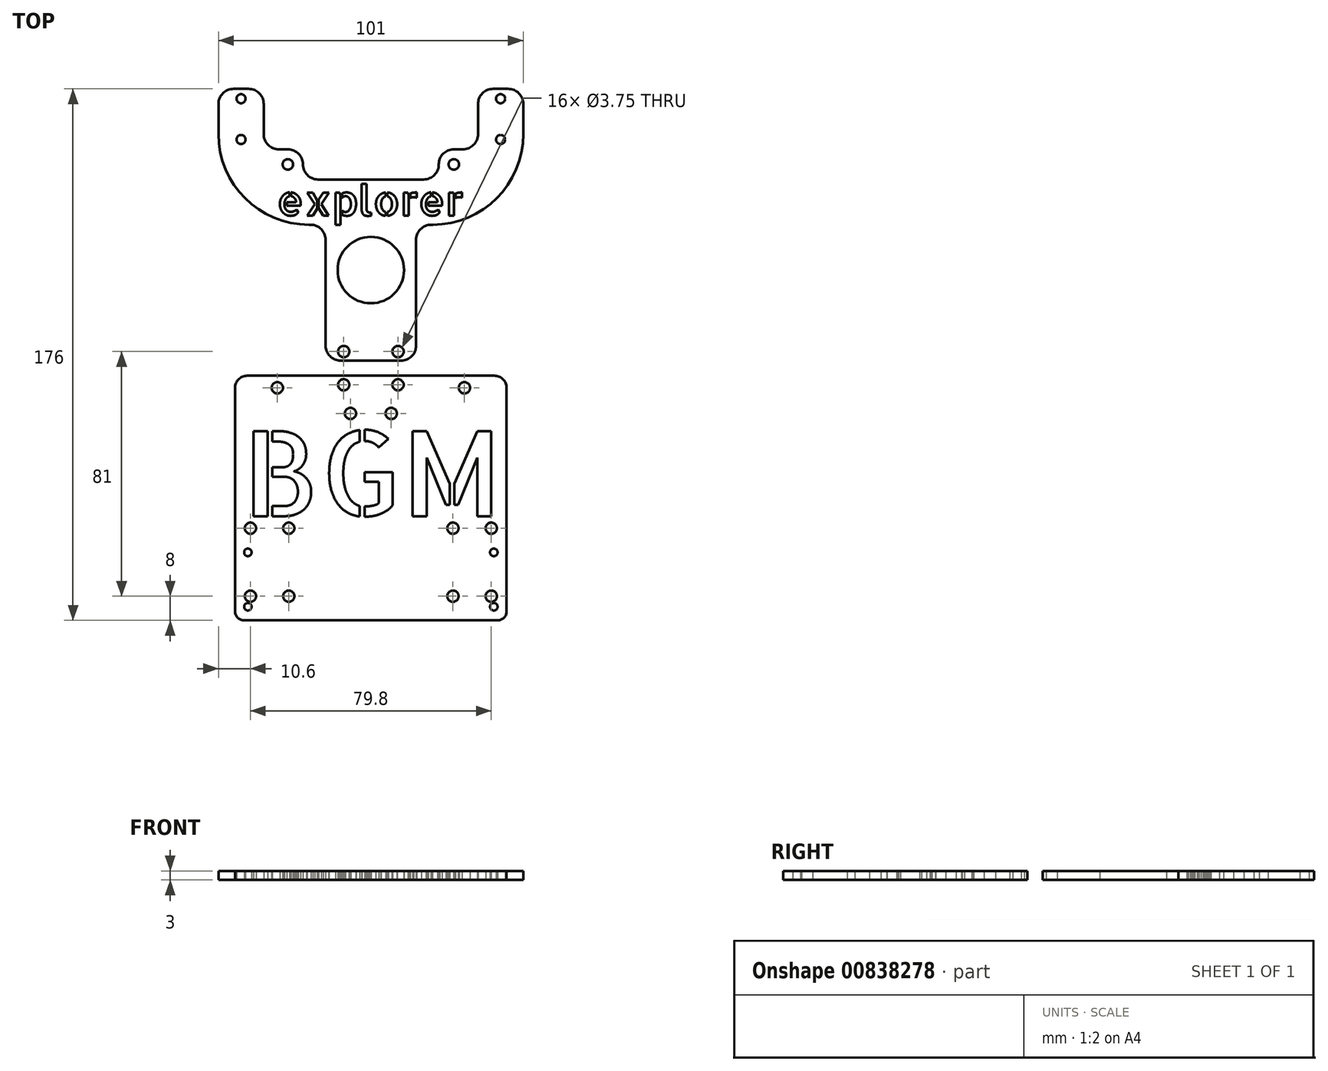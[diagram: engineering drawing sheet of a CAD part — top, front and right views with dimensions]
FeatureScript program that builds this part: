
annotation { "Feature Type Name" : "Feature", "Feature Type Description" : "" }
export const myFeature = defineFeature(function(context is Context, id is Id, definition is map)
    precondition{}
    {
        {
            var Q0;
            Q0=qCreatedBy(makeId("Top.planeOp"),FACE);
            var sketch = newSketch(context, id + "F0", { "sketchPlane" : qUnion([Q0])});
            skLineSegment(sketch, "E0.bottom", {"start": v(-45, -40.5) * mm, "end": v(45, -40.5) * mm});
            skLineSegment(sketch, "E0.top", {"start": v(-45, 40.5) * mm, "end": v(45, 40.5) * mm});
            skLineSegment(sketch, "E0.left", {"start": v(-45, -40.5) * mm, "end": v(-45, 40.5) * mm});
            skLineSegment(sketch, "E0.right", {"start": v(45, -40.5) * mm, "end": v(45, 40.5) * mm});
            skPoint(sketch, "E0.middle", {"position": v(0, 0) * mm});
            skCircle(sketch, "E1", {"center": v(-39.9, -32.5) * mm, "radius": 1.88 * mm});
            skCircle(sketch, "E2", {"center": v(-39.9, -10) * mm, "radius": 1.88 * mm});
            skCircle(sketch, "E3", {"center": v(-27.2, -10) * mm, "radius": 1.88 * mm});
            skCircle(sketch, "E4", {"center": v(-27.2, -32.5) * mm, "radius": 1.88 * mm});
            skCircle(sketch, "E5", {"center": v(-9, 37.5) * mm, "radius": 1.88 * mm});
            skCircle(sketch, "E6", {"center": v(-31, 36.5) * mm, "radius": 1.88 * mm});
            skLineSegment(sketch, "E7", {"start": v(0, 40.5) * mm, "end": v(0, -40.5) * mm, "construction": true});
            skCircle(sketch, "E8.MirrorC", {"center": v(27.2, -32.5) * mm, "radius": 1.88 * mm});
            skCircle(sketch, "E9.MirrorC", {"center": v(27.2, -10) * mm, "radius": 1.88 * mm});
            skCircle(sketch, "E10.MirrorC", {"center": v(39.9, -32.5) * mm, "radius": 1.88 * mm});
            skCircle(sketch, "E11.MirrorC", {"center": v(31, 36.5) * mm, "radius": 1.88 * mm});
            skCircle(sketch, "E12.MirrorC", {"center": v(39.9, -10) * mm, "radius": 1.88 * mm});
            skCircle(sketch, "E13.MirrorC", {"center": v(9, 37.5) * mm, "radius": 1.88 * mm});
            skText(sketch, "E14", { "text": "BGM", "fontName": "AllertaStencil-Regular.ttf"});
            skCircle(sketch, "E15", {"center": v(-6.75, 28) * mm, "radius": 1.88 * mm});
            skCircle(sketch, "E16.MirrorC", {"center": v(6.75, 28) * mm, "radius": 1.88 * mm});
            skCircle(sketch, "E17", {"center": v(-40.75, -36) * mm, "radius": 1.25 * mm});
            skCircle(sketch, "E18", {"center": v(-40.75, -18) * mm, "radius": 1.25 * mm});
            skCircle(sketch, "E19.MirrorC", {"center": v(40.75, -18) * mm, "radius": 1.25 * mm});
            skCircle(sketch, "E20.MirrorC", {"center": v(40.75, -36) * mm, "radius": 1.25 * mm});
            const initialGuessF0  = {"E14": [-0.0425, -0.006, 1, 0, 0.0282]};
            skSetInitialGuess(sketch, initialGuessF0);
            skSolve(sketch);
        }
        {
            var Q0;
            Q0=makeQuery(id+"F0.imprint","IMPRINT",FACE,{"disambiguationData":[TD([[makeQuery(id+"F0.imprint","IMPRINT",EDGE,{"derivedFrom":sQuery(id+"F0.wireOp",EDGE,"E0.bottom")}),1.0]])]});
            var Q1;
            {var subQ5=sQuery(id+"F0.wireOp",EDGE,"2Zm90AiD-Dhtj-uD5s-axWy-PgKTOK4LKh8v.bottom");Q1=makeQuery(id+"F0.imprint","IMPRINT",FACE,{"disambiguationData":[TD([[makeQuery(id+"F0.imprint","IMPRINT",EDGE,{"derivedFrom":subQ5}),1.0]])]});}
            var Q2;
            {var subQ0=sQuery(id+"F0.wireOp",EDGE,"E14.sketch_text.stroke-19");Q2=makeQuery(id+"F0.imprint","IMPRINT",FACE,{"disambiguationData":[TD([[makeQuery(id+"F0.imprint","IMPRINT",EDGE,{"derivedFrom":subQ0}),1.0]])]});}
            var Q3;
            {var subQ1=sQuery(id+"F0.wireOp",EDGE,"E14.sketch_text.stroke-21");Q3=makeQuery(id+"F0.imprint","IMPRINT",FACE,{"disambiguationData":[TD([[makeQuery(id+"F0.imprint","IMPRINT",EDGE,{"derivedFrom":subQ1}),1.0]])]});}
            var Q4;
            {var subQ1=sQuery(id+"F0.wireOp",EDGE,"E14.sketch_text.stroke-17");Q4=makeQuery(id+"F0.imprint","IMPRINT",FACE,{"disambiguationData":[TD([[makeQuery(id+"F0.imprint","IMPRINT",EDGE,{"derivedFrom":subQ1}),1.0]])]});}
            var Q5;
            {var subQ1=sQuery(id+"F0.wireOp",EDGE,"E14.sketch_text.stroke-13");Q5=makeQuery(id+"F0.imprint","IMPRINT",FACE,{"disambiguationData":[TD([[makeQuery(id+"F0.imprint","IMPRINT",EDGE,{"derivedFrom":subQ1}),1.0]])]});}
            var Q6;
            {var subQ1=sQuery(id+"F0.wireOp",EDGE,"2Zm90AiD-Dhtj-uD5s-axWy-PgKTOK4LKh8v.top");Q6=makeQuery(id+"F0.imprint","IMPRINT",FACE,{"disambiguationData":[TD([[makeQuery(id+"F0.imprint","IMPRINT",EDGE,{"derivedFrom":subQ1}),-1.0]])]});}
            extrude(context, id + "F1", {"entities" : qUnion([Q0, Q1, Q2, Q3, Q4, Q5, Q6]), "depth" : 3 * mm, "offsetDistance" : 25 * mm});
        }
        {
            var Q0;
            Q0=makeQuery(id+"F1.opExtrude","SWEPT_EDGE",EDGE,{"disambiguationData":[OSD([sQuery(id+"F0.wireOp",EDGE,"E0.top"),sQuery(id+"F0.wireOp",EDGE,"EnCkEkhA-jMUl-QUfc-oNYT-XxU6Z7l8rYp0")])]});
            var Q1;
            Q1=makeQuery(id+"F1.opExtrude","SWEPT_EDGE",EDGE,{"disambiguationData":[OSD([sQuery(id+"F0.wireOp",EDGE,"QOfj2mfs-kfRg-gTgU-dF6D-Hk0wWBTF9spk"),sQuery(id+"F0.wireOp",EDGE,"EnCkEkhA-jMUl-QUfc-oNYT-XxU6Z7l8rYp0")])]});
            var Q2;
            Q2=makeQuery(id+"F1.opExtrude","SWEPT_EDGE",EDGE,{"disambiguationData":[OSD([sQuery(id+"F0.wireOp",EDGE,"E0.top"),sQuery(id+"F0.wireOp",EDGE,"c5541e3c-3a26-47a1-8419-0039d4e5da4d0.MirrorCS")])]});
            var Q3;
            Q3=makeQuery(id+"F1.opExtrude","SWEPT_EDGE",EDGE,{"disambiguationData":[OSD([sQuery(id+"F0.wireOp",EDGE,"c5541e3c-3a26-47a1-8419-0039d4e5da4d0.MirrorCS"),sQuery(id+"F0.wireOp",EDGE,"c5541e3c-3a26-47a1-8419-0039d4e5da4d1.MirrorCS")])]});
            fillet(context, id + "F2", {"entities" : qUnion([Q0, Q1, Q2, Q3]), "radius" : 4 * mm, "tangentPropagation" : true, "allowEdgeOverflow" : false});
        }
        {
            var Q0;
            Q0=makeQuery(id+"F1.opExtrude","SWEPT_EDGE",EDGE,{"disambiguationData":[OSD([sQuery(id+"F0.wireOp",EDGE,"E0.bottom"),sQuery(id+"F0.wireOp",EDGE,"E0.left")])]});
            var Q1;
            Q1=makeQuery(id+"F1.opExtrude","SWEPT_EDGE",EDGE,{"disambiguationData":[OSD([sQuery(id+"F0.wireOp",EDGE,"E0.bottom"),sQuery(id+"F0.wireOp",EDGE,"E0.right")])]});
            fillet(context, id + "F3", {"entities" : qUnion([Q0, Q1]), "radius" : 3 * mm, "tangentPropagation" : true, "allowEdgeOverflow" : false});
        }
        {
            var Q0;
            Q0=qCreatedBy(makeId("Top.planeOp"),FACE);
            var sketch = newSketch(context, id + "F4", { "sketchPlane" : qUnion([Q0])});
            skLineSegment(sketch, "E21", {"start": v(-22.5, 115.5) * mm, "end": v(-35.5, 115.5) * mm});
            skLineSegment(sketch, "E22", {"start": v(35.5, 115.5) * mm, "end": v(22.5, 115.5) * mm});
            skLineSegment(sketch, "E23", {"start": v(22.5, 115.5) * mm, "end": v(22.5, 105.5) * mm});
            skLineSegment(sketch, "E24", {"start": v(22.5, 105.5) * mm, "end": v(0, 105.5) * mm});
            skLineSegment(sketch, "E25", {"start": v(-22.5, 105.5) * mm, "end": v(-22.5, 115.5) * mm});
            skLineSegment(sketch, "E26", {"start": v(0, 105.5) * mm, "end": v(-22.5, 105.5) * mm});
            skCircle(sketch, "E27", {"center": v(-27.5, 110.5) * mm, "radius": 1.75 * mm});
            skCircle(sketch, "E28", {"center": v(27.5, 110.5) * mm, "radius": 1.75 * mm});
            skCircle(sketch, "E29", {"center": v(0, 75.5) * mm, "radius": 11 * mm});
            skLineSegment(sketch, "E30", {"start": v(0, 75.5) * mm, "end": v(0, 105.5) * mm, "construction": true});
            skLineSegment(sketch, "E31", {"start": v(0, 75.5) * mm, "end": v(0, 45.5) * mm, "construction": true});
            skLineSegment(sketch, "E32.0", {"start": v(-41, 40.5) * mm, "end": v(0, 40.5) * mm});
            skCircle(sketch, "E33.0", {"center": v(-9, 37.5) * mm, "radius": 1.88 * mm});
            skCircle(sketch, "E34.0", {"center": v(9, 37.5) * mm, "radius": 1.88 * mm});
            skCircle(sketch, "E35", {"center": v(-9, 48.5) * mm, "radius": 1.88 * mm});
            skCircle(sketch, "E36", {"center": v(9, 48.5) * mm, "radius": 1.88 * mm});
            skLineSegment(sketch, "E37", {"start": v(0, 45.5) * mm, "end": v(-15, 45.5) * mm});
            skLineSegment(sketch, "E38", {"start": v(0, 45.5) * mm, "end": v(15, 45.5) * mm});
            skLineSegment(sketch, "E39", {"start": v(0, 40.5) * mm, "end": v(41, 40.5) * mm});
            skLineSegment(sketch, "E40", {"start": v(-15, 45.5) * mm, "end": v(-15, 90.5) * mm});
            skLineSegment(sketch, "E41", {"start": v(-15, 90.5) * mm, "end": v(-50.5, 90.5) * mm});
            skLineSegment(sketch, "E42", {"start": v(-50.5, 90.5) * mm, "end": v(-50.5, 135.5) * mm});
            skLineSegment(sketch, "E43", {"start": v(-35.5, 115.5) * mm, "end": v(-35.5, 135.5) * mm});
            skLineSegment(sketch, "E44", {"start": v(-35.5, 135.5) * mm, "end": v(-50.5, 135.5) * mm});
            skLineSegment(sketch, "E45", {"start": v(35.5, 115.5) * mm, "end": v(35.5, 135.5) * mm});
            skLineSegment(sketch, "E46", {"start": v(35.5, 135.5) * mm, "end": v(50.5, 135.5) * mm});
            skLineSegment(sketch, "E47", {"start": v(50.5, 135.5) * mm, "end": v(50.5, 90.5) * mm});
            skLineSegment(sketch, "E48", {"start": v(50.5, 90.5) * mm, "end": v(15, 90.5) * mm});
            skLineSegment(sketch, "E49", {"start": v(15, 90.5) * mm, "end": v(15, 45.5) * mm});
            skCircle(sketch, "E50", {"center": v(-43, 132.25) * mm, "radius": 1.5 * mm});
            skPoint(sketch, "E50.centerSnap0", {"position": v(-43, 135.5) * mm});
            skCircle(sketch, "E51", {"center": v(-43, 118.75) * mm, "radius": 1.5 * mm});
            skCircle(sketch, "E52.MirrorC", {"center": v(43, 132.25) * mm, "radius": 1.5 * mm});
            skCircle(sketch, "E53.MirrorC", {"center": v(43, 118.75) * mm, "radius": 1.5 * mm});
            skText(sketch, "E54", { "text": "explorer", "fontName": "AllertaStencil-Regular.ttf"});
            const initialGuessF4  = {"E54": [-0.03113, 0.0935, 1, 0, 0.01]};
            skSetInitialGuess(sketch, initialGuessF4);
            skSolve(sketch);
        }
        {
            var Q0;
            Q0=makeQuery(id+"F4.imprint","IMPRINT",FACE,{"disambiguationData":[TD([[makeQuery(id+"F4.imprint","IMPRINT",EDGE,{"derivedFrom":sQuery(id+"F4.wireOp",EDGE,"E21")}),1.0]])]});
            extrude(context, id + "F5", {"entities" : qUnion([Q0]), "depth" : 3 * mm, "offsetDistance" : 25 * mm});
        }
        {
            var Q0;
            Q0=makeQuery(id+"F5.opExtrude","SWEPT_EDGE",EDGE,{"disambiguationData":[OSD([sQuery(id+"F4.wireOp",EDGE,"E41"),sQuery(id+"F4.wireOp",EDGE,"E42")])]});
            var Q1;
            Q1=makeQuery(id+"F5.opExtrude","SWEPT_EDGE",EDGE,{"disambiguationData":[OSD([sQuery(id+"F4.wireOp",EDGE,"E47"),sQuery(id+"F4.wireOp",EDGE,"E48")])]});
            fillet(context, id + "F6", {"entities" : qUnion([Q0, Q1]), "radius" : 30 * mm, "tangentPropagation" : true, "allowEdgeOverflow" : false});
        }
        {
            var Q0;
            Q0=makeQuery(id+"F5.opExtrude","SWEPT_EDGE",EDGE,{"disambiguationData":[OSD([sQuery(id+"F4.wireOp",EDGE,"E40"),sQuery(id+"F4.wireOp",EDGE,"E41")])]});
            var Q1;
            Q1=makeQuery(id+"F5.opExtrude","SWEPT_EDGE",EDGE,{"disambiguationData":[OSD([sQuery(id+"F4.wireOp",EDGE,"E48"),sQuery(id+"F4.wireOp",EDGE,"E49")])]});
            var Q2;
            Q2=makeQuery(id+"F5.opExtrude","SWEPT_EDGE",EDGE,{"disambiguationData":[OSD([sQuery(id+"F4.wireOp",EDGE,"E25"),sQuery(id+"F4.wireOp",EDGE,"E26")])]});
            var Q3;
            Q3=makeQuery(id+"F5.opExtrude","SWEPT_EDGE",EDGE,{"disambiguationData":[OSD([sQuery(id+"F4.wireOp",EDGE,"E21"),sQuery(id+"F4.wireOp",EDGE,"E43")])]});
            var Q4;
            Q4=makeQuery(id+"F5.opExtrude","SWEPT_EDGE",EDGE,{"disambiguationData":[OSD([sQuery(id+"F4.wireOp",EDGE,"E21"),sQuery(id+"F4.wireOp",EDGE,"E25")])]});
            var Q5;
            Q5=makeQuery(id+"F5.opExtrude","SWEPT_EDGE",EDGE,{"disambiguationData":[OSD([sQuery(id+"F4.wireOp",EDGE,"E22"),sQuery(id+"F4.wireOp",EDGE,"E45")])]});
            var Q6;
            Q6=makeQuery(id+"F5.opExtrude","SWEPT_EDGE",EDGE,{"disambiguationData":[OSD([sQuery(id+"F4.wireOp",EDGE,"E22"),sQuery(id+"F4.wireOp",EDGE,"E23")])]});
            var Q7;
            Q7=makeQuery(id+"F5.opExtrude","SWEPT_EDGE",EDGE,{"disambiguationData":[OSD([sQuery(id+"F4.wireOp",EDGE,"E23"),sQuery(id+"F4.wireOp",EDGE,"E24")])]});
            var Q8;
            Q8=makeQuery(id+"F5.opExtrude","SWEPT_EDGE",EDGE,{"disambiguationData":[OSD([sQuery(id+"F4.wireOp",EDGE,"E45"),sQuery(id+"F4.wireOp",EDGE,"E46")])]});
            var Q9;
            Q9=makeQuery(id+"F5.opExtrude","SWEPT_EDGE",EDGE,{"disambiguationData":[OSD([sQuery(id+"F4.wireOp",EDGE,"E46"),sQuery(id+"F4.wireOp",EDGE,"E47")])]});
            var Q10;
            Q10=makeQuery(id+"F5.opExtrude","SWEPT_EDGE",EDGE,{"disambiguationData":[OSD([sQuery(id+"F4.wireOp",EDGE,"E42"),sQuery(id+"F4.wireOp",EDGE,"E44")])]});
            var Q11;
            Q11=makeQuery(id+"F5.opExtrude","SWEPT_EDGE",EDGE,{"disambiguationData":[OSD([sQuery(id+"F4.wireOp",EDGE,"E43"),sQuery(id+"F4.wireOp",EDGE,"E44")])]});
            var Q12;
            Q12=makeQuery(id+"F5.opExtrude","SWEPT_EDGE",EDGE,{"disambiguationData":[OSD([sQuery(id+"F4.wireOp",EDGE,"E37"),sQuery(id+"F4.wireOp",EDGE,"E40")])]});
            var Q13;
            Q13=makeQuery(id+"F5.opExtrude","SWEPT_EDGE",EDGE,{"disambiguationData":[OSD([sQuery(id+"F4.wireOp",EDGE,"E38"),sQuery(id+"F4.wireOp",EDGE,"E49")])]});
            fillet(context, id + "F7", {"entities" : qUnion([Q0, Q1, Q2, Q3, Q4, Q5, Q6, Q7, Q8, Q9, Q10, Q11, Q12, Q13]), "radius" : 5 * mm, "tangentPropagation" : true, "allowEdgeOverflow" : false});
        }
    });
